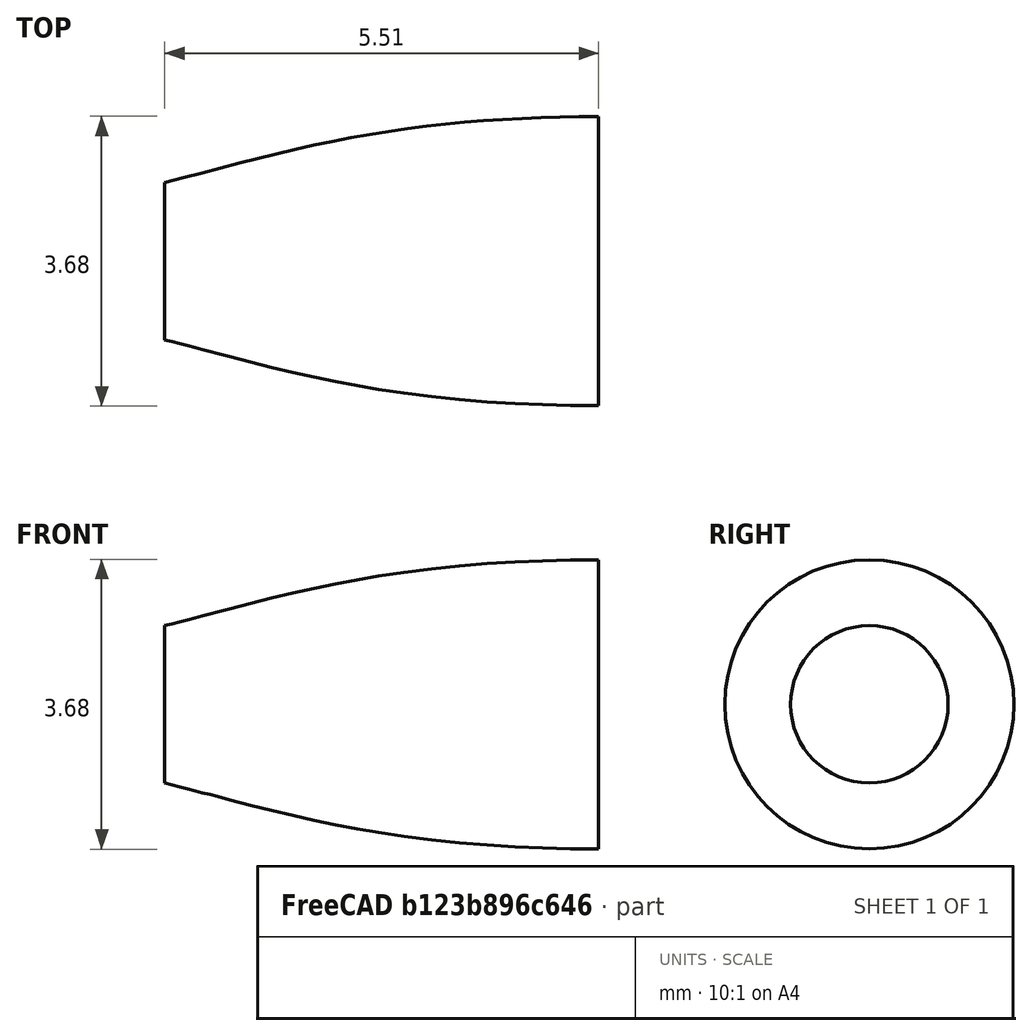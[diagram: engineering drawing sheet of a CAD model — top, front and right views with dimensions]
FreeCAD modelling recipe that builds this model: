
FCSTD DOCUMENT  (FreeCAD 0.21R33771 (Git))
Label: NozzleCAD
License: All rights reserved
LicenseURL: http://en.wikipedia.org/wiki/All_rights_reserved
objects: Points::Feature×1, Part::FeaturePython×1, Part::Revolution×1
note: 2 computed .brp shape members not serialized (recipe doc carries the construction recipe); baked Part::Feature solids carry a one-line shape summary decoded from their .brp

FEATURE [Points::Feature] nozzleContour
FEATURE [Part::FeaturePython] Approximation_Curve  # WARN: FeaturePython — macro-defined, semantics opaque (R4)
  ApproxTolerance = 0.001
  ClampEnds = false
  Closed = false
  Continuity = 3
  CurvatureWeight = 1
  DegreeMax = 5
  DegreeMin = 3
  FirstIndex = 0
  LastIndex = -1
  LengthWeight = 1
  Method = 0
  Parametrization = 0
  PointObject = -> nozzleContour
  StartOffset = 0
  TorsionWeight = 1
FEATURE [Part::Revolution] Revolve
  Angle = 360
  Axis = (1,0,0)
  Base = (0,0,0)
  FaceMakerClass = Part::FaceMakerBullseye
  Solid = false
  Source = -> Approximation_Curve
  Symmetric = false
